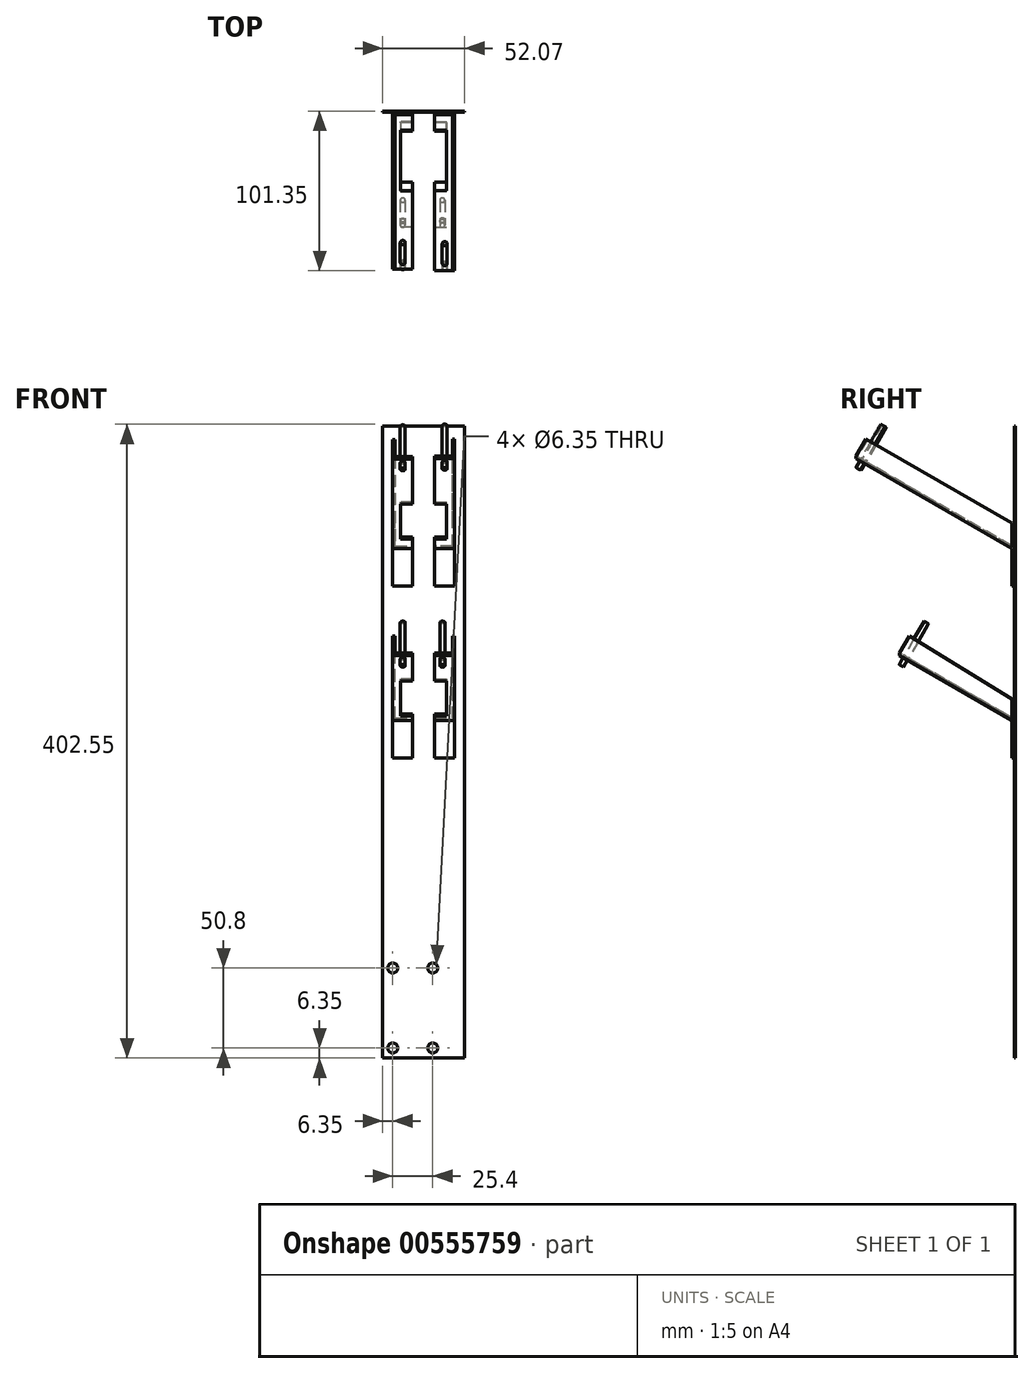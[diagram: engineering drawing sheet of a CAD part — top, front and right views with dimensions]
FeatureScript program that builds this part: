
annotation { "Feature Type Name" : "Feature", "Feature Type Description" : "" }
export const myFeature = defineFeature(function(context is Context, id is Id, definition is map)
    precondition{}
    {
        {
            var Q0;
            Q0=qCreatedBy(makeId("Front.planeOp"),FACE);
            var sketch = newSketch(context, id + "F0", { "sketchPlane" : qUnion([Q0])});
            skLineSegment(sketch, "E0.bottom", {"start": v(0, 0) * mm, "end": v(-38.1, 0) * mm});
            skLineSegment(sketch, "E0.top", {"start": v(0, -401.32) * mm, "end": v(-38.1, -401.32) * mm});
            skLineSegment(sketch, "E0.left", {"start": v(0, 0) * mm, "end": v(0, -401.32) * mm});
            skLineSegment(sketch, "E0.right", {"start": v(-38.1, 0) * mm, "end": v(-38.1, -401.32) * mm});
            skSolve(sketch);
        }
        {
            var Q0;
            Q0=makeQuery(id+"F0.imprint","IMPRINT",FACE,{"disambiguationData":[TD([[makeQuery(id+"F0.imprint","IMPRINT",EDGE,{"derivedFrom":sQuery(id+"F0.wireOp",EDGE,"E0.bottom")}),1.0]])]});
            extrude(context, id + "F1", {"entities" : qUnion([Q0]), "depth" : 0.64 * mm, "offsetDistance" : 25.4 * mm});
        }
        {
            var Q0;
            Q0=makeQuery(id+"F1.opExtrude","SWEPT_FACE",FACE,{"disambiguationData":[OSD([sQuery(id+"F0.wireOp",EDGE,"E0.left")])]});
            extrude(context, id + "F2", {"entities" : qUnion([Q0]), "operationType" : NewBodyOperationType.ADD, "depth" : 13.97 * mm, "offsetDistance" : 25.4 * mm});
        }
        {
            var Q0;
            {var subQ0=sQuery(id+"F0.wireOp",EDGE,"E0.left");Q0=makeQuery(id+"F2.boolean.opBoolean","MERGE",FACE,{"derivedFrom":[makeQuery(id+"F1.opExtrude","CAP_FACE",FACE,{"disambiguationData":[OSD([sQuery(id+"F0.wireOp",EDGE,"E0.bottom"),sQuery(id+"F0.wireOp",EDGE,"E0.top"),subQ0,sQuery(id+"F0.wireOp",EDGE,"E0.right")])],"isStart":false}),makeQuery(id+"F2.opExtrude","SWEPT_FACE",FACE,{"disambiguationData":[OSD([subQ0]),TDD([makeQuery(id+"F1.opExtrude","CAP_EDGE",EDGE,{"disambiguationData":[OSD([subQ0])],"isStart":false})])]})]});}
            var sketch = newSketch(context, id + "F3", { "sketchPlane" : qUnion([Q0])});
            skLineSegment(sketch, "E1.bottom", {"start": v(7.62, -76.2) * mm, "end": v(-5.08, -76.2) * mm});
            skLineSegment(sketch, "E1.top", {"start": v(7.62, -101.6) * mm, "end": v(-5.08, -101.6) * mm});
            skLineSegment(sketch, "E1.left", {"start": v(7.62, -76.2) * mm, "end": v(7.62, -101.6) * mm});
            skLineSegment(sketch, "E1.right", {"start": v(-5.08, -76.2) * mm, "end": v(-5.08, -101.6) * mm});
            skSolve(sketch);
        }
        {
            var Q0;
            Q0 = qSketchRegion(id + "F3", true);
            extrude(context, id + "F4", {"entities" : qUnion([Q0]), "operationType" : NewBodyOperationType.ADD, "depth" : 1.52 * mm, "offsetDistance" : 25.4 * mm});
        }
        {
            var Q0;
            {var subQ0=sQuery(id+"F0.wireOp",EDGE,"E0.left");Q0=makeQuery(id+"F2.boolean.opBoolean","MERGE",FACE,{"derivedFrom":[makeQuery(id+"F1.opExtrude","CAP_FACE",FACE,{"disambiguationData":[OSD([sQuery(id+"F0.wireOp",EDGE,"E0.bottom"),sQuery(id+"F0.wireOp",EDGE,"E0.top"),subQ0,sQuery(id+"F0.wireOp",EDGE,"E0.right")])],"isStart":false}),makeQuery(id+"F2.opExtrude","SWEPT_FACE",FACE,{"disambiguationData":[OSD([subQ0]),TDD([makeQuery(id+"F1.opExtrude","CAP_EDGE",EDGE,{"disambiguationData":[OSD([subQ0])],"isStart":false})])]})]});}
            var sketch = newSketch(context, id + "F5", { "sketchPlane" : qUnion([Q0])});
            skLineSegment(sketch, "E2.bottom", {"start": v(-31.75, -76.2) * mm, "end": v(-19.05, -76.2) * mm});
            skLineSegment(sketch, "E2.top", {"start": v(-31.75, -101.6) * mm, "end": v(-19.05, -101.6) * mm});
            skLineSegment(sketch, "E2.left", {"start": v(-31.75, -76.2) * mm, "end": v(-31.75, -101.6) * mm});
            skLineSegment(sketch, "E2.right", {"start": v(-19.05, -76.2) * mm, "end": v(-19.05, -101.6) * mm});
            skSolve(sketch);
        }
        {
            var Q0;
            Q0 = qSketchRegion(id + "F5", true);
            extrude(context, id + "F6", {"entities" : qUnion([Q0]), "operationType" : NewBodyOperationType.ADD, "depth" : 1.52 * mm, "offsetDistance" : 25.4 * mm});
        }
        {
            var Q0;
            Q0=makeQuery(id+"F4.opExtrude","SWEPT_FACE",FACE,{"disambiguationData":[OSD([sQuery(id+"F3.wireOp",EDGE,"E1.left")])]});
            var sketch = newSketch(context, id + "F7", { "sketchPlane" : qUnion([Q0])});
            skLineSegment(sketch, "E3", {"start": v(-2.16, -76.2) * mm, "end": v(-101.15, -19.05) * mm});
            skLineSegment(sketch, "E4", {"start": v(-101.15, -19.05) * mm, "end": v(-101.15, -20.57) * mm});
            skLineSegment(sketch, "E5", {"start": v(-101.15, -20.57) * mm, "end": v(-2.16, -77.72) * mm});
            skLineSegment(sketch, "E6", {"start": v(-2.16, -76.2) * mm, "end": v(-2.16, -77.72) * mm});
            skSolve(sketch);
        }
        {
            var Q0;
            Q0 = qSketchRegion(id + "F7", true);
            extrude(context, id + "F8", {"entities" : qUnion([Q0]), "operationType" : NewBodyOperationType.ADD, "oppositeDirection" : true, "depth" : 12.7 * mm, "offsetDistance" : 25.4 * mm});
        }
        {
            var Q0;
            Q0=makeQuery(id+"F6.opExtrude","SWEPT_FACE",FACE,{"disambiguationData":[OSD([sQuery(id+"F5.wireOp",EDGE,"E2.left")])]});
            var sketch = newSketch(context, id + "F9", { "sketchPlane" : qUnion([Q0])});
            skLineSegment(sketch, "E7", {"start": v(2.16, -76.2) * mm, "end": v(2.16, -77.72) * mm});
            skLineSegment(sketch, "E8", {"start": v(2.16, -77.72) * mm, "end": v(100.48, -20.96) * mm});
            skLineSegment(sketch, "E9", {"start": v(100.48, -20.96) * mm, "end": v(100.48, -19.43) * mm});
            skLineSegment(sketch, "E10", {"start": v(100.48, -19.43) * mm, "end": v(2.16, -76.2) * mm});
            skLineSegment(sketch, "E11", {"start": v(2.16, -77.72) * mm, "end": v(2.16, -76.2) * mm});
            skSolve(sketch);
        }
        {
            var Q0;
            Q0 = qSketchRegion(id + "F9", true);
            extrude(context, id + "F10", {"entities" : qUnion([Q0]), "operationType" : NewBodyOperationType.ADD, "oppositeDirection" : true, "depth" : 12.7 * mm, "offsetDistance" : 25.4 * mm});
        }
        {
            var Q0;
            Q0=makeQuery(id+"F8.boolean.opBoolean","MERGE",FACE,{"derivedFrom":[makeQuery(id+"F4.opExtrude","SWEPT_FACE",FACE,{"disambiguationData":[OSD([sQuery(id+"F3.wireOp",EDGE,"E1.left")])]}),makeQuery(id+"F8.opExtrude","CAP_FACE",FACE,{"disambiguationData":[OSD([sQuery(id+"F7.wireOp",EDGE,"E3"),sQuery(id+"F7.wireOp",EDGE,"E4"),sQuery(id+"F7.wireOp",EDGE,"E5"),sQuery(id+"F7.wireOp",EDGE,"E6")])],"isStart":true})]});
            var sketch = newSketch(context, id + "F11", { "sketchPlane" : qUnion([Q0])});
            skLineSegment(sketch, "E12", {"start": v(-2.16, -76.2) * mm, "end": v(-2.16, -61.54) * mm});
            skLineSegment(sketch, "E13", {"start": v(-2.16, -61.54) * mm, "end": v(-94.8, -8.05) * mm});
            skLineSegment(sketch, "E14", {"start": v(-94.8, -8.05) * mm, "end": v(-101.15, -19.05) * mm});
            skLineSegment(sketch, "E15", {"start": v(-101.15, -19.05) * mm, "end": v(-2.16, -76.2) * mm});
            skSolve(sketch);
        }
        {
            var Q0;
            Q0 = qSketchRegion(id + "F11", true);
            extrude(context, id + "F12", {"entities" : qUnion([Q0]), "operationType" : NewBodyOperationType.ADD, "oppositeDirection" : true, "depth" : 1.52 * mm, "offsetDistance" : 25.4 * mm});
        }
        {
            var Q0;
            Q0=makeQuery(id+"F10.boolean.opBoolean","MERGE",FACE,{"derivedFrom":[makeQuery(id+"F6.opExtrude","SWEPT_FACE",FACE,{"disambiguationData":[OSD([sQuery(id+"F5.wireOp",EDGE,"E2.left")])]}),makeQuery(id+"F10.opExtrude","CAP_FACE",FACE,{"disambiguationData":[OSD([sQuery(id+"F9.wireOp",EDGE,"E8"),sQuery(id+"F9.wireOp",EDGE,"E9"),sQuery(id+"F9.wireOp",EDGE,"E10"),sQuery(id+"F9.wireOp",EDGE,"E11")])],"isStart":true})]});
            var sketch = newSketch(context, id + "F13", { "sketchPlane" : qUnion([Q0])});
            skLineSegment(sketch, "E16", {"start": v(2.16, -76.2) * mm, "end": v(2.16, -61.54) * mm});
            skLineSegment(sketch, "E17", {"start": v(2.16, -61.54) * mm, "end": v(94.13, -8.44) * mm});
            skLineSegment(sketch, "E18", {"start": v(94.13, -8.44) * mm, "end": v(100.48, -19.43) * mm});
            skLineSegment(sketch, "E19", {"start": v(100.48, -19.43) * mm, "end": v(2.16, -76.2) * mm});
            skSolve(sketch);
        }
        {
            var Q0;
            Q0 = qSketchRegion(id + "F13", true);
            extrude(context, id + "F14", {"entities" : qUnion([Q0]), "operationType" : NewBodyOperationType.ADD, "oppositeDirection" : true, "depth" : 1.52 * mm, "offsetDistance" : 25.4 * mm});
        }
        {
            var Q0;
            Q0=makeQuery(id+"F10.opExtrude","SWEPT_FACE",FACE,{"disambiguationData":[OSD([sQuery(id+"F9.wireOp",EDGE,"E10")])]});
            var sketch = newSketch(context, id + "F15", { "sketchPlane" : qUnion([Q0])});
            skLineSegment(sketch, "E20.bottom", {"start": v(-19.05, 24.85) * mm, "end": v(-26.67, 24.85) * mm});
            skLineSegment(sketch, "E20.top", {"start": v(-19.05, -19.6) * mm, "end": v(-26.67, -19.6) * mm});
            skLineSegment(sketch, "E20.left", {"start": v(-19.05, 24.85) * mm, "end": v(-19.05, -19.6) * mm});
            skLineSegment(sketch, "E20.right", {"start": v(-26.67, 24.85) * mm, "end": v(-26.67, -19.6) * mm});
            skLineSegment(sketch, "E21.bottom", {"start": v(-5.08, 24.85) * mm, "end": v(2.54, 24.85) * mm});
            skLineSegment(sketch, "E21.top", {"start": v(-5.08, -19.6) * mm, "end": v(2.54, -19.6) * mm});
            skLineSegment(sketch, "E21.left", {"start": v(-5.08, 24.85) * mm, "end": v(-5.08, -19.6) * mm});
            skLineSegment(sketch, "E21.right", {"start": v(2.54, 24.85) * mm, "end": v(2.54, -19.6) * mm});
            skSolve(sketch);
        }
        {
            var Q0;
            Q0 = qSketchRegion(id + "F15", true);
            extrude(context, id + "F16", {"entities" : qUnion([Q0]), "operationType" : NewBodyOperationType.REMOVE, "oppositeDirection" : true, "depth" : 25.4 * mm, "offsetDistance" : 25.4 * mm});
        }
        {
            var Q0;
            {var subQ0=sQuery(id+"F0.wireOp",EDGE,"E0.left");Q0=makeQuery(id+"F2.boolean.opBoolean","MERGE",FACE,{"derivedFrom":[makeQuery(id+"F1.opExtrude","CAP_FACE",FACE,{"disambiguationData":[OSD([sQuery(id+"F0.wireOp",EDGE,"E0.bottom"),sQuery(id+"F0.wireOp",EDGE,"E0.top"),subQ0,sQuery(id+"F0.wireOp",EDGE,"E0.right")])],"isStart":false}),makeQuery(id+"F2.opExtrude","SWEPT_FACE",FACE,{"disambiguationData":[OSD([subQ0]),TDD([makeQuery(id+"F1.opExtrude","CAP_EDGE",EDGE,{"disambiguationData":[OSD([subQ0])],"isStart":false})])]})]});}
            var sketch = newSketch(context, id + "F17", { "sketchPlane" : qUnion([Q0])});
            skLineSegment(sketch, "E22.bottom", {"start": v(-31.75, -185.42) * mm, "end": v(-19.05, -185.42) * mm});
            skLineSegment(sketch, "E22.top", {"start": v(-31.75, -210.82) * mm, "end": v(-19.05, -210.82) * mm});
            skLineSegment(sketch, "E22.left", {"start": v(-31.75, -185.42) * mm, "end": v(-31.75, -210.82) * mm});
            skLineSegment(sketch, "E22.right", {"start": v(-19.05, -185.42) * mm, "end": v(-19.05, -210.82) * mm});
            skLineSegment(sketch, "E23.bottom", {"start": v(-5.08, -185.42) * mm, "end": v(7.62, -185.42) * mm});
            skLineSegment(sketch, "E23.top", {"start": v(-5.08, -210.82) * mm, "end": v(7.62, -210.82) * mm});
            skLineSegment(sketch, "E23.left", {"start": v(-5.08, -185.42) * mm, "end": v(-5.08, -210.82) * mm});
            skLineSegment(sketch, "E23.right", {"start": v(7.62, -185.42) * mm, "end": v(7.62, -210.82) * mm});
            skSolve(sketch);
        }
        {
            var Q0;
            Q0 = qSketchRegion(id + "F17", true);
            extrude(context, id + "F18", {"entities" : qUnion([Q0]), "operationType" : NewBodyOperationType.ADD, "depth" : 1.52 * mm, "offsetDistance" : 25.4 * mm});
        }
        {
            var Q0;
            Q0=makeQuery(id+"F12.boolean.opBoolean","MERGE",FACE,{"derivedFrom":[makeQuery(id+"F8.boolean.opBoolean","MERGE",FACE,{"derivedFrom":[makeQuery(id+"F4.opExtrude","SWEPT_FACE",FACE,{"disambiguationData":[OSD([sQuery(id+"F3.wireOp",EDGE,"E1.left")])]}),makeQuery(id+"F8.opExtrude","CAP_FACE",FACE,{"disambiguationData":[OSD([sQuery(id+"F7.wireOp",EDGE,"E3"),sQuery(id+"F7.wireOp",EDGE,"E4"),sQuery(id+"F7.wireOp",EDGE,"E5"),sQuery(id+"F7.wireOp",EDGE,"E6")])],"isStart":true})]}),makeQuery(id+"F12.opExtrude","CAP_FACE",FACE,{"disambiguationData":[OSD([sQuery(id+"F11.wireOp",EDGE,"E12"),sQuery(id+"F11.wireOp",EDGE,"E13"),sQuery(id+"F11.wireOp",EDGE,"E14"),sQuery(id+"F11.wireOp",EDGE,"E15")])],"isStart":true})]});
            var sketch = newSketch(context, id + "F19", { "sketchPlane" : qUnion([Q0])});
            skLineSegment(sketch, "E24", {"start": v(-2.16, -185.42) * mm, "end": v(-73.65, -144.15) * mm});
            skLineSegment(sketch, "E25", {"start": v(-73.65, -144.15) * mm, "end": v(-73.65, -145.67) * mm});
            skLineSegment(sketch, "E26", {"start": v(-73.65, -145.67) * mm, "end": v(-2.16, -186.94) * mm});
            skLineSegment(sketch, "E27", {"start": v(-2.16, -186.94) * mm, "end": v(-2.16, -185.42) * mm});
            skSolve(sketch);
        }
        {
            var Q0;
            Q0 = qSketchRegion(id + "F19", true);
            extrude(context, id + "F20", {"entities" : qUnion([Q0]), "operationType" : NewBodyOperationType.ADD, "oppositeDirection" : true, "depth" : 12.7 * mm, "offsetDistance" : 25.4 * mm});
        }
        {
            var Q0;
            Q0=makeQuery(id+"F18.opExtrude","SWEPT_FACE",FACE,{"disambiguationData":[OSD([sQuery(id+"F17.wireOp",EDGE,"E22.left")])]});
            var sketch = newSketch(context, id + "F21", { "sketchPlane" : qUnion([Q0])});
            skLineSegment(sketch, "E28", {"start": v(2.16, -185.42) * mm, "end": v(73.65, -144.15) * mm});
            skLineSegment(sketch, "E29", {"start": v(73.65, -144.15) * mm, "end": v(73.65, -145.67) * mm});
            skLineSegment(sketch, "E30", {"start": v(73.65, -145.67) * mm, "end": v(2.16, -186.94) * mm});
            skLineSegment(sketch, "E31", {"start": v(2.16, -185.42) * mm, "end": v(2.16, -186.94) * mm});
            skSolve(sketch);
        }
        {
            var Q0;
            Q0 = qSketchRegion(id + "F21", true);
            extrude(context, id + "F22", {"entities" : qUnion([Q0]), "operationType" : NewBodyOperationType.ADD, "oppositeDirection" : true, "depth" : 12.7 * mm, "offsetDistance" : 25.4 * mm});
        }
        {
            var Q0;
            Q0=makeQuery(id+"F12.boolean.opBoolean","MERGE",FACE,{"derivedFrom":[makeQuery(id+"F8.boolean.opBoolean","MERGE",FACE,{"derivedFrom":[makeQuery(id+"F4.opExtrude","SWEPT_FACE",FACE,{"disambiguationData":[OSD([sQuery(id+"F3.wireOp",EDGE,"E1.left")])]}),makeQuery(id+"F8.opExtrude","CAP_FACE",FACE,{"disambiguationData":[OSD([sQuery(id+"F7.wireOp",EDGE,"E3"),sQuery(id+"F7.wireOp",EDGE,"E4"),sQuery(id+"F7.wireOp",EDGE,"E5"),sQuery(id+"F7.wireOp",EDGE,"E6")])],"isStart":true})]}),makeQuery(id+"F12.opExtrude","CAP_FACE",FACE,{"disambiguationData":[OSD([sQuery(id+"F11.wireOp",EDGE,"E12"),sQuery(id+"F11.wireOp",EDGE,"E13"),sQuery(id+"F11.wireOp",EDGE,"E14"),sQuery(id+"F11.wireOp",EDGE,"E15")])],"isStart":true})]});
            var sketch = newSketch(context, id + "F23", { "sketchPlane" : qUnion([Q0])});
            skLineSegment(sketch, "E32", {"start": v(-2.16, -185.42) * mm, "end": v(-2.16, -173.2) * mm});
            skLineSegment(sketch, "E33", {"start": v(-2.16, -173.2) * mm, "end": v(-67.3, -133.15) * mm});
            skLineSegment(sketch, "E34", {"start": v(-67.3, -133.15) * mm, "end": v(-73.65, -144.15) * mm});
            skLineSegment(sketch, "E35", {"start": v(-73.65, -144.15) * mm, "end": v(-2.16, -185.42) * mm});
            skSolve(sketch);
        }
        {
            var Q0;
            Q0 = qSketchRegion(id + "F23", true);
            extrude(context, id + "F24", {"entities" : qUnion([Q0]), "operationType" : NewBodyOperationType.ADD, "oppositeDirection" : true, "depth" : 1.52 * mm, "offsetDistance" : 25.4 * mm});
        }
        {
            var Q0;
            Q0=makeQuery(id+"F22.boolean.opBoolean","MERGE",FACE,{"derivedFrom":[makeQuery(id+"F18.opExtrude","SWEPT_FACE",FACE,{"disambiguationData":[OSD([sQuery(id+"F17.wireOp",EDGE,"E22.left")])]}),makeQuery(id+"F22.opExtrude","CAP_FACE",FACE,{"disambiguationData":[OSD([sQuery(id+"F21.wireOp",EDGE,"E28"),sQuery(id+"F21.wireOp",EDGE,"E29"),sQuery(id+"F21.wireOp",EDGE,"E30"),sQuery(id+"F21.wireOp",EDGE,"E31")])],"isStart":true})]});
            var sketch = newSketch(context, id + "F25", { "sketchPlane" : qUnion([Q0])});
            skLineSegment(sketch, "E36", {"start": v(2.16, -185.42) * mm, "end": v(2.16, -173.22) * mm});
            skLineSegment(sketch, "E37", {"start": v(2.16, -173.22) * mm, "end": v(67.3, -133.15) * mm});
            skLineSegment(sketch, "E38", {"start": v(67.3, -133.15) * mm, "end": v(73.65, -144.15) * mm});
            skLineSegment(sketch, "E39", {"start": v(73.65, -144.15) * mm, "end": v(2.16, -185.42) * mm});
            skSolve(sketch);
        }
        {
            var Q0;
            Q0 = qSketchRegion(id + "F25", true);
            extrude(context, id + "F26", {"entities" : qUnion([Q0]), "operationType" : NewBodyOperationType.ADD, "oppositeDirection" : true, "depth" : 1.52 * mm, "offsetDistance" : 25.4 * mm});
        }
        {
            var Q0;
            Q0=makeQuery(id+"F22.opExtrude","SWEPT_FACE",FACE,{"disambiguationData":[OSD([sQuery(id+"F21.wireOp",EDGE,"E28")])]});
            var sketch = newSketch(context, id + "F27", { "sketchPlane" : qUnion([Q0])});
            skLineSegment(sketch, "E40.bottom", {"start": v(-19.05, 85.76) * mm, "end": v(-26.67, 85.76) * mm});
            skLineSegment(sketch, "E40.top", {"start": v(-19.05, 41.31) * mm, "end": v(-26.67, 41.31) * mm});
            skLineSegment(sketch, "E40.left", {"start": v(-19.05, 85.76) * mm, "end": v(-19.05, 41.31) * mm});
            skLineSegment(sketch, "E40.right", {"start": v(-26.67, 85.76) * mm, "end": v(-26.67, 41.31) * mm});
            skLineSegment(sketch, "E41.bottom", {"start": v(-5.08, 41.31) * mm, "end": v(2.54, 41.31) * mm});
            skLineSegment(sketch, "E41.top", {"start": v(-5.08, 85.76) * mm, "end": v(2.54, 85.76) * mm});
            skLineSegment(sketch, "E41.left", {"start": v(-5.08, 41.31) * mm, "end": v(-5.08, 85.76) * mm});
            skLineSegment(sketch, "E41.right", {"start": v(2.54, 41.31) * mm, "end": v(2.54, 85.76) * mm});
            skSolve(sketch);
        }
        {
            var Q0;
            Q0 = qSketchRegion(id + "F27", true);
            extrude(context, id + "F28", {"entities" : qUnion([Q0]), "operationType" : NewBodyOperationType.REMOVE, "oppositeDirection" : true, "depth" : 25.4 * mm, "offsetDistance" : 25.4 * mm});
        }
        {
            var Q0;
            {var subQ0=sQuery(id+"F0.wireOp",EDGE,"E0.left");Q0=makeQuery(id+"F2.boolean.opBoolean","MERGE",FACE,{"derivedFrom":[makeQuery(id+"F1.opExtrude","CAP_FACE",FACE,{"disambiguationData":[OSD([sQuery(id+"F0.wireOp",EDGE,"E0.bottom"),sQuery(id+"F0.wireOp",EDGE,"E0.top"),subQ0,sQuery(id+"F0.wireOp",EDGE,"E0.right")])],"isStart":false}),makeQuery(id+"F2.opExtrude","SWEPT_FACE",FACE,{"disambiguationData":[OSD([subQ0]),TDD([makeQuery(id+"F1.opExtrude","CAP_EDGE",EDGE,{"disambiguationData":[OSD([subQ0])],"isStart":false})])]})]});}
            var sketch = newSketch(context, id + "F29", { "sketchPlane" : qUnion([Q0])});
            skCircle(sketch, "E42", {"center": v(-31.75, -394.97) * mm, "radius": 3.18 * mm});
            skCircle(sketch, "E43", {"center": v(-31.75, -344.17) * mm, "radius": 3.18 * mm});
            skCircle(sketch, "E44", {"center": v(-6.35, -344.17) * mm, "radius": 3.18 * mm});
            skCircle(sketch, "E45", {"center": v(-6.35, -394.97) * mm, "radius": 3.18 * mm});
            skSolve(sketch);
        }
        {
            var Q0;
            Q0 = qSketchRegion(id + "F29", true);
            extrude(context, id + "F30", {"entities" : qUnion([Q0]), "operationType" : NewBodyOperationType.REMOVE, "oppositeDirection" : true, "depth" : 25.4 * mm, "offsetDistance" : 25.4 * mm});
        }
        {
            var Q0;
            Q0=makeQuery(id+"F10.opExtrude","SWEPT_FACE",FACE,{"disambiguationData":[OSD([sQuery(id+"F9.wireOp",EDGE,"E10")])]});
            var sketch = newSketch(context, id + "F31", { "sketchPlane" : qUnion([Q0])});
            skCircle(sketch, "E46", {"center": v(-25.4, -72.28) * mm, "radius": 1.59 * mm});
            skCircle(sketch, "E47", {"center": v(1.27, -73.05) * mm, "radius": 1.59 * mm});
            skSolve(sketch);
        }
        {
            var Q0;
            Q0 = qSketchRegion(id + "F31", true);
            extrude(context, id + "F32", {"entities" : qUnion([Q0]), "operationType" : NewBodyOperationType.ADD, "depth" : 25.4 * mm, "offsetDistance" : 25.4 * mm, "hasSecondDirection" : true, "secondDirectionOppositeDirection" : true, "secondDirectionDepth" : 6.35 * mm});
        }
        {
            var Q0;
            Q0=makeQuery(id+"F22.opExtrude","SWEPT_FACE",FACE,{"disambiguationData":[OSD([sQuery(id+"F21.wireOp",EDGE,"E28")])]});
            var sketch = newSketch(context, id + "F33", { "sketchPlane" : qUnion([Q0])});
            skCircle(sketch, "E48", {"center": v(-25.4, 13.37) * mm, "radius": 1.59 * mm});
            skCircle(sketch, "E49", {"center": v(-0.25, 13.37) * mm, "radius": 1.59 * mm});
            skSolve(sketch);
        }
        {
            var Q0;
            Q0 = qSketchRegion(id + "F33", true);
            extrude(context, id + "F34", {"entities" : qUnion([Q0]), "operationType" : NewBodyOperationType.ADD, "depth" : 25.4 * mm, "offsetDistance" : 25.4 * mm, "hasSecondDirection" : true, "secondDirectionOppositeDirection" : true, "secondDirectionDepth" : 6.35 * mm});
        }
    });
